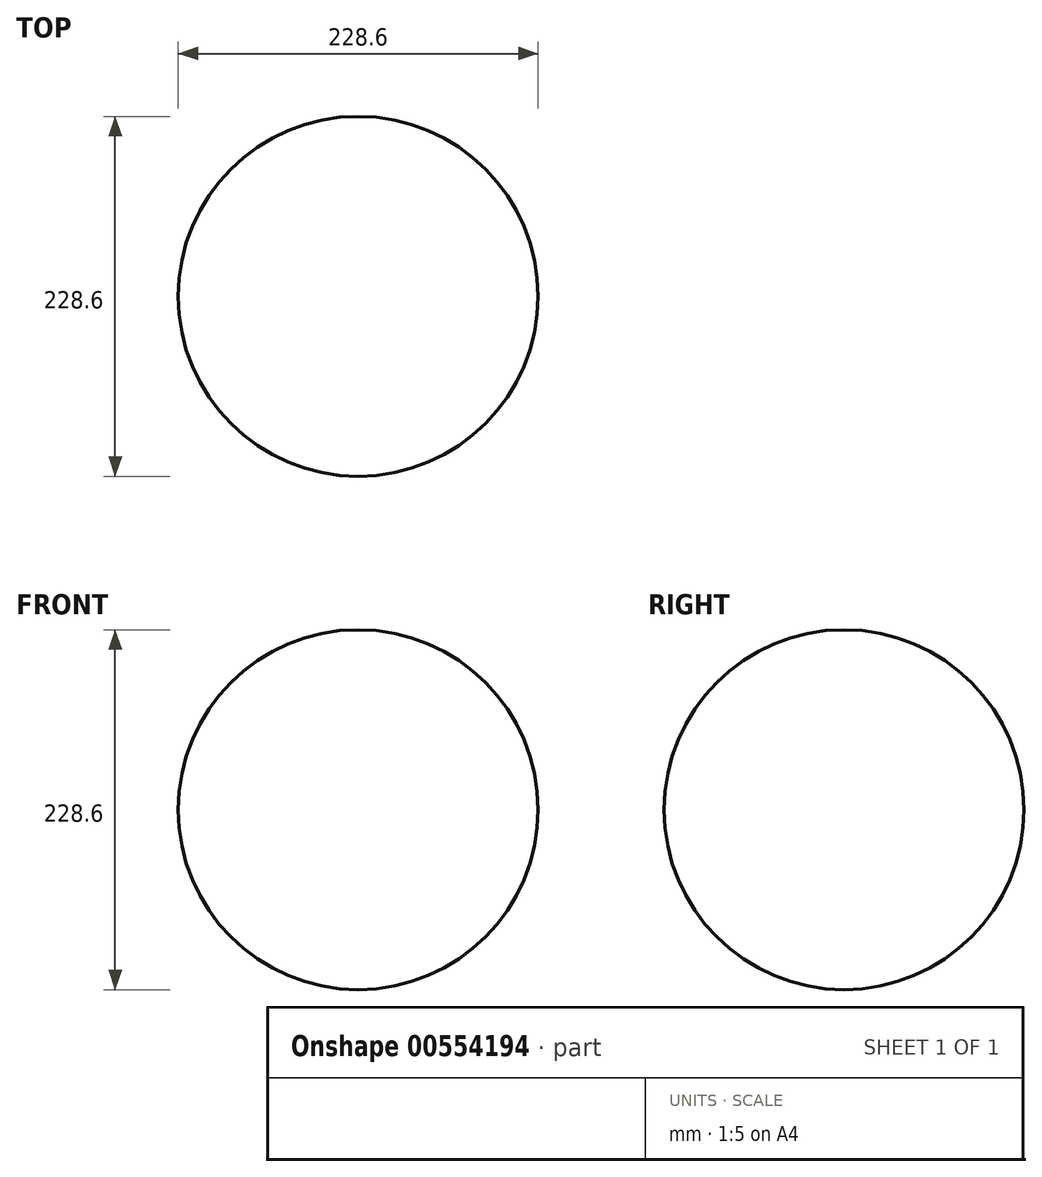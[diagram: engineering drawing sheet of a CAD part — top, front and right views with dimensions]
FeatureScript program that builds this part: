
annotation { "Feature Type Name" : "Feature", "Feature Type Description" : "" }
export const myFeature = defineFeature(function(context is Context, id is Id, definition is map)
    precondition{}
    {
        {
            var Q0;
            Q0=qCreatedBy(makeId("Front.planeOp"),FACE);
            var sketch = newSketch(context, id + "F0", { "sketchPlane" : qUnion([Q0])});
            skCircle(sketch, "E0", {"center": v(0, 0) * mm, "radius": 114.3 * mm});
            skLineSegment(sketch, "E1", {"start": v(-114.3, 0) * mm, "end": v(114.3, 0) * mm});
            skSolve(sketch);
        }
        {
            var Q0;
            {var subQ0=sQuery(id+"F0.wireOp",EDGE,"E1");Q0=makeQuery(id+"F0.imprint","IMPRINT",FACE,{"disambiguationData":[TD([[makeQuery(id+"F0.imprint","IMPRINT",EDGE,{"derivedFrom":subQ0}),1.0]])]});}
            var Q1;
            Q1=sQuery(id+"F0.wireOp",EDGE,"E1");
            revolve(context, id + "F1", {"entities" : qUnion([Q0]), "axis" : qUnion([Q1]), "revolveType" : RevolveType.FULL});
        }
    });
